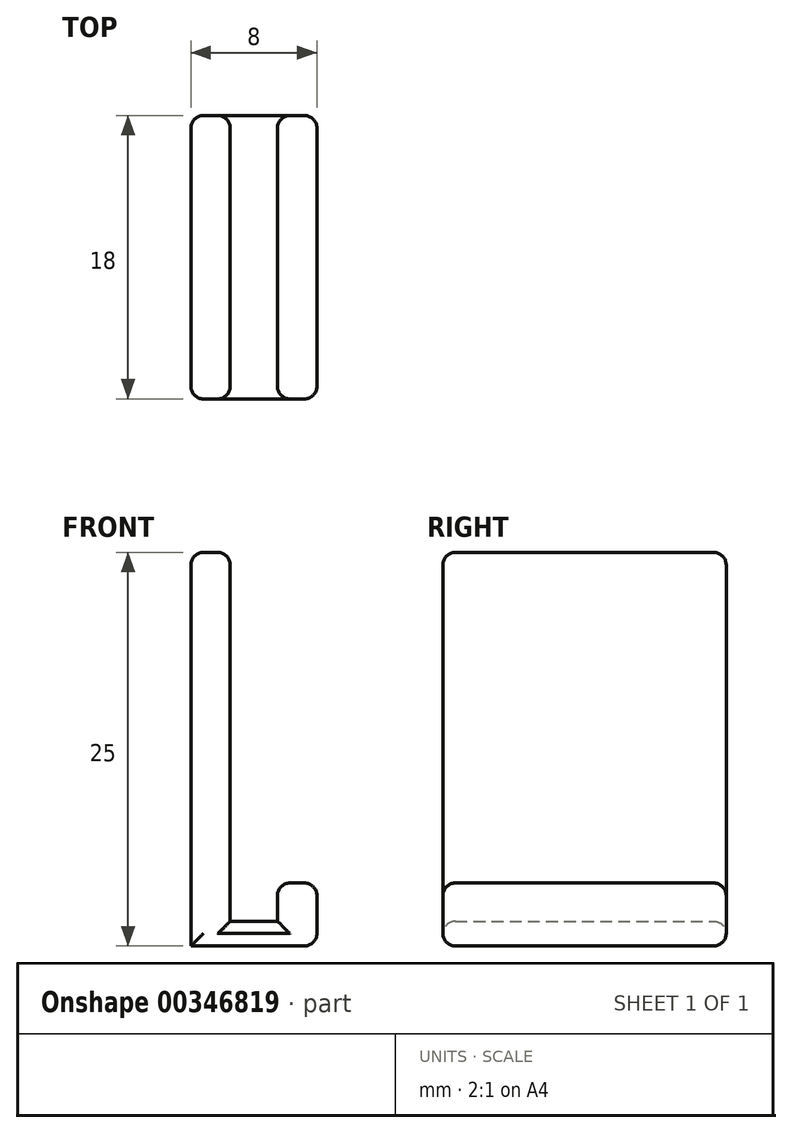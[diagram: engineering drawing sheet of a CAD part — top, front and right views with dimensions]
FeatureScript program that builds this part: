
annotation { "Feature Type Name" : "Feature", "Feature Type Description" : "" }
export const myFeature = defineFeature(function(context is Context, id is Id, definition is map)
    precondition{}
    {
        {
            var Q0;
            Q0=qCreatedBy(makeId("Front.planeOp"),FACE);
            var sketch = newSketch(context, id + "F0", { "sketchPlane" : qUnion([Q0])});
            skLineSegment(sketch, "E0.bottom", {"start": v(0, 0) * mm, "end": v(2.5, 0) * mm});
            skLineSegment(sketch, "E0.top", {"start": v(0, 25) * mm, "end": v(2.5, 25) * mm});
            skLineSegment(sketch, "E0.left", {"start": v(0, 0) * mm, "end": v(0, 25) * mm});
            skLineSegment(sketch, "E0.right", {"start": v(2.5, 0) * mm, "end": v(2.5, 25) * mm});
            skLineSegment(sketch, "E1.bottom", {"start": v(0, 0) * mm, "end": v(8, 0) * mm});
            skLineSegment(sketch, "E1.top", {"start": v(0, 1.57) * mm, "end": v(8, 1.57) * mm});
            skLineSegment(sketch, "E1.left", {"start": v(0, 0) * mm, "end": v(0, 1.57) * mm});
            skLineSegment(sketch, "E1.right", {"start": v(8, 0) * mm, "end": v(8, 1.57) * mm});
            skLineSegment(sketch, "E2.bottom", {"start": v(8, 0) * mm, "end": v(5.5, 0) * mm});
            skLineSegment(sketch, "E2.top", {"start": v(8, 4) * mm, "end": v(5.5, 4) * mm});
            skLineSegment(sketch, "E2.left", {"start": v(8, 0) * mm, "end": v(8, 4) * mm});
            skLineSegment(sketch, "E2.right", {"start": v(5.5, 0) * mm, "end": v(5.5, 4) * mm});
            skSolve(sketch);
        }
        {
            var Q0;
            Q0 = qSketchRegion(id + "F0", true);
            extrude(context, id + "F1", {"entities" : qUnion([Q0]), "depth" : 18 * mm});
        }
        {
            var Q0;
            Q0=makeQuery(id+"F1.opExtrude","SWEPT_EDGE",EDGE,{"disambiguationData":[OSD([sQuery(id+"F0.wireOp",EDGE,"E2.top"),sQuery(id+"F0.wireOp",EDGE,"E2.left")])]});
            var Q1;
            Q1=makeQuery(id+"F1.opExtrude","CAP_EDGE",EDGE,{"disambiguationData":[OSD([sQuery(id+"F0.wireOp",EDGE,"E0.right")])],"isStart":false});
            var Q2;
            Q2=makeQuery(id+"F1.opExtrude","CAP_EDGE",EDGE,{"disambiguationData":[OSD([sQuery(id+"F0.wireOp",EDGE,"E1.top")])],"isStart":false});
            var Q3;
            Q3=makeQuery(id+"F1.opExtrude","CAP_EDGE",EDGE,{"disambiguationData":[OSD([sQuery(id+"F0.wireOp",EDGE,"E2.right")])],"isStart":false});
            var Q4;
            Q4=makeQuery(id+"F1.opExtrude","CAP_EDGE",EDGE,{"disambiguationData":[OSD([sQuery(id+"F0.wireOp",EDGE,"E2.top")])],"isStart":false});
            var Q5;
            Q5=makeQuery(id+"F1.opExtrude","CAP_EDGE",EDGE,{"disambiguationData":[OSD([sQuery(id+"F0.wireOp",EDGE,"E2.left")])],"isStart":false});
            var Q6;
            Q6=makeQuery(id+"F1.opExtrude","CAP_EDGE",EDGE,{"disambiguationData":[OSD([sQuery(id+"F0.wireOp",EDGE,"E1.bottom"),sQuery(id+"F0.wireOp",EDGE,"E2.bottom")])],"isStart":false});
            var Q7;
            Q7=makeQuery(id+"F1.opExtrude","CAP_EDGE",EDGE,{"disambiguationData":[OSD([sQuery(id+"F0.wireOp",EDGE,"E0.left"),sQuery(id+"F0.wireOp",EDGE,"E1.left")])],"isStart":false});
            var Q8;
            Q8=makeQuery(id+"F1.opExtrude","SWEPT_EDGE",EDGE,{"disambiguationData":[OSD([sQuery(id+"F0.wireOp",EDGE,"E2.bottom"),sQuery(id+"F0.wireOp",EDGE,"E2.left")])]});
            var Q9;
            Q9=makeQuery(id+"F1.opExtrude","SWEPT_EDGE",EDGE,{"disambiguationData":[OSD([sQuery(id+"F0.wireOp",EDGE,"E2.top"),sQuery(id+"F0.wireOp",EDGE,"E2.right")])]});
            var Q10;
            Q10=makeQuery(id+"F1.opExtrude","CAP_EDGE",EDGE,{"disambiguationData":[OSD([sQuery(id+"F0.wireOp",EDGE,"E2.top")])],"isStart":true});
            var Q11;
            Q11=makeQuery(id+"F1.opExtrude","CAP_EDGE",EDGE,{"disambiguationData":[OSD([sQuery(id+"F0.wireOp",EDGE,"E2.right")])],"isStart":true});
            var Q12;
            Q12=makeQuery(id+"F1.opExtrude","CAP_EDGE",EDGE,{"disambiguationData":[OSD([sQuery(id+"F0.wireOp",EDGE,"E1.top")])],"isStart":true});
            var Q13;
            Q13=makeQuery(id+"F1.opExtrude","CAP_EDGE",EDGE,{"disambiguationData":[OSD([sQuery(id+"F0.wireOp",EDGE,"E1.bottom"),sQuery(id+"F0.wireOp",EDGE,"E2.bottom")])],"isStart":true});
            var Q14;
            Q14=makeQuery(id+"F1.opExtrude","CAP_EDGE",EDGE,{"disambiguationData":[OSD([sQuery(id+"F0.wireOp",EDGE,"E2.left")])],"isStart":true});
            var Q15;
            Q15=makeQuery(id+"F1.opExtrude","CAP_EDGE",EDGE,{"disambiguationData":[OSD([sQuery(id+"F0.wireOp",EDGE,"E0.right")])],"isStart":true});
            var Q16;
            Q16=makeQuery(id+"F1.opExtrude","CAP_EDGE",EDGE,{"disambiguationData":[OSD([sQuery(id+"F0.wireOp",EDGE,"E0.left"),sQuery(id+"F0.wireOp",EDGE,"E1.left")])],"isStart":true});
            var Q17;
            Q17=makeQuery(id+"F1.opExtrude","SWEPT_EDGE",EDGE,{"disambiguationData":[OSD([sQuery(id+"F0.wireOp",EDGE,"E0.top"),sQuery(id+"F0.wireOp",EDGE,"E0.right")])]});
            var Q18;
            Q18=makeQuery(id+"F1.opExtrude","CAP_EDGE",EDGE,{"disambiguationData":[OSD([sQuery(id+"F0.wireOp",EDGE,"E0.top")])],"isStart":true});
            var Q19;
            Q19=makeQuery(id+"F1.opExtrude","CAP_EDGE",EDGE,{"disambiguationData":[OSD([sQuery(id+"F0.wireOp",EDGE,"E0.top")])],"isStart":false});
            var Q20;
            Q20=makeQuery(id+"F1.opExtrude","SWEPT_EDGE",EDGE,{"disambiguationData":[OSD([sQuery(id+"F0.wireOp",EDGE,"E0.top"),sQuery(id+"F0.wireOp",EDGE,"E0.left")])]});
            var Q21;
            Q21=makeQuery(id+"F1.opExtrude","SWEPT_EDGE",EDGE,{"disambiguationData":[OSD([sQuery(id+"F0.wireOp",EDGE,"E1.bottom"),sQuery(id+"F0.wireOp",EDGE,"E1.left")])]});
            fillet(context, id + "F2", {"entities" : qUnion([Q0, Q1, Q2, Q3, Q4, Q5, Q6, Q7, Q8, Q9, Q10, Q11, Q12, Q13, Q14, Q15, Q16, Q17, Q18, Q19, Q20, Q21]), "radius" : 0.8 * mm, "tangentPropagation" : true, "allowEdgeOverflow" : false});
        }
    });
